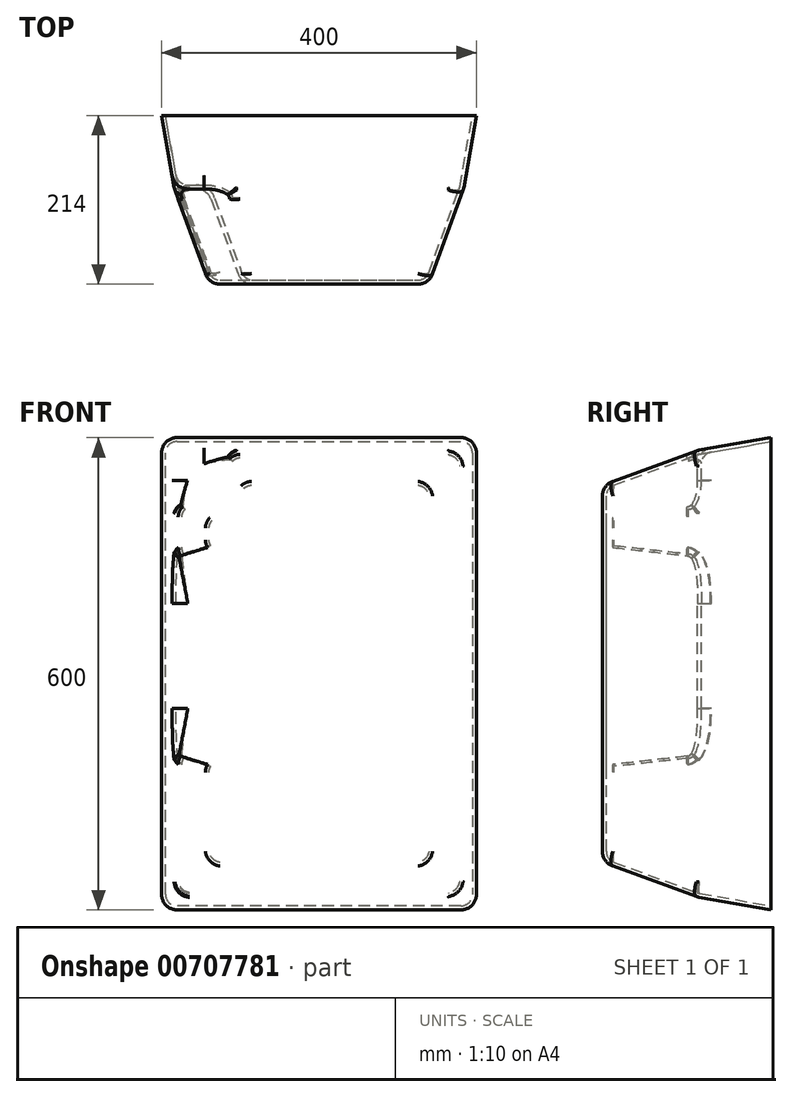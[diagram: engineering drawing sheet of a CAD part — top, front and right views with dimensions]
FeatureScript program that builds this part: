
annotation { "Feature Type Name" : "Feature", "Feature Type Description" : "" }
export const myFeature = defineFeature(function(context is Context, id is Id, definition is map)
    precondition{}
    {
        {
            var Q0;
            Q0=qCreatedBy(makeId("Front.planeOp"),FACE);
            var sketch = newSketch(context, id + "F0", { "sketchPlane" : qUnion([Q0])});
            skCircle(sketch, "E0", {"center": v(0, 0) * mm, "radius": 100 * mm});
            skLineSegment(sketch, "E1.bottom", {"start": v(-200, 300) * mm, "end": v(200, 300) * mm});
            skLineSegment(sketch, "E1.top", {"start": v(-200, -300) * mm, "end": v(200, -300) * mm});
            skLineSegment(sketch, "E1.left", {"start": v(-200, 300) * mm, "end": v(-200, -300) * mm});
            skLineSegment(sketch, "E1.right", {"start": v(200, 300) * mm, "end": v(200, -300) * mm});
            skSolve(sketch);
        }
        {
            var Q0;
            Q0=makeQuery(id+"F0.imprint","IMPRINT",FACE,{"disambiguationData":[TD([[makeQuery(id+"F0.imprint","IMPRINT",EDGE,{"derivedFrom":sQuery(id+"F0.wireOp",EDGE,"E0")}),-1.0]])]});
            var Q1;
            Q1=makeQuery(id+"F0.imprint","IMPRINT",FACE,{"disambiguationData":[TD([[makeQuery(id+"F0.imprint","IMPRINT",EDGE,{"derivedFrom":sQuery(id+"F0.wireOp",EDGE,"E0")}),1.0]])]});
            extrude(context, id + "F1", {"entities" : qUnion([Q0, Q1]), "depth" : 93 * mm, "offsetDistance" : 25 * mm, "hasDraft" : true, "draftAngle" : 10 * degree, "draftPullDirection" : true});
        }
        {
            var Q0;
            Q0=makeQuery(id+"F1.opExtrude","CAP_FACE",FACE,{"disambiguationData":[OSD([sQuery(id+"F0.wireOp",EDGE,"E1.bottom"),sQuery(id+"F0.wireOp",EDGE,"E1.top"),sQuery(id+"F0.wireOp",EDGE,"E1.left"),sQuery(id+"F0.wireOp",EDGE,"E1.right")])],"isStart":false});
            var sketch = newSketch(context, id + "F2", { "sketchPlane" : qUnion([Q0])});
            skLineSegment(sketch, "E2", {"start": v(-209.11, 182.83) * mm, "end": v(-67.8, 326.25) * mm});
            skLineSegment(sketch, "E3", {"start": v(99.21, 69.27) * mm, "end": v(99.21, -109.47) * mm});
            skLineSegment(sketch, "E4", {"start": v(-122.2, -49.55) * mm, "end": v(19.1, 93.87) * mm});
            skCircle(sketch, "E5", {"center": v(-72.45, -175.48) * mm, "radius": 40.45 * mm});
            skCircle(sketch, "E6", {"center": v(-367.03, 22.56) * mm, "radius": 67.26 * mm});
            skCircle(sketch, "E7", {"center": v(-367.03, 22.56) * mm, "radius": 225 * mm});
            skSolve(sketch);
        }
        {
            var Q0;
            Q0=makeQuery(id+"F2.imprint","IMPRINT",FACE,{"disambiguationData":[TD([[makeQuery(id+"F2.imprint","IMPRINT",EDGE,{"derivedFrom":sQuery(id+"F2.wireOp",EDGE,"E5")}),-1.0]])]});
            var Q1;
            Q1=makeQuery(id+"F2.imprint","IMPRINT",FACE,{"disambiguationData":[TD([[makeQuery(id+"F2.imprint","IMPRINT",EDGE,{"derivedFrom":sQuery(id+"F2.wireOp",EDGE,"E5")}),1.0]])]});
            extrude(context, id + "F3", {"entities" : qUnion([Q0, Q1]), "operationType" : NewBodyOperationType.ADD, "depth" : 121 * mm, "offsetDistance" : 25 * mm, "hasDraft" : true, "draftAngle" : 20 * degree, "draftPullDirection" : true});
        }
        {
            var Q0;
            Q0=makeQuery(id+"F3.opExtrude","CAP_FACE",FACE,{"disambiguationData":[OSD([sQuery(id+"F0.wireOp",EDGE,"E1.bottom"),sQuery(id+"F0.wireOp",EDGE,"E1.top"),sQuery(id+"F0.wireOp",EDGE,"E1.left"),sQuery(id+"F0.wireOp",EDGE,"E1.right"),sQuery(id+"F2.wireOp",EDGE,"E2"),sQuery(id+"F2.wireOp",EDGE,"E7")])],"isStart":false});
            var Q1;
            Q1=makeQuery(id+"F1.opExtrude","SWEPT_EDGE",EDGE,{"disambiguationData":[OSD([sQuery(id+"F0.wireOp",EDGE,"E1.top"),sQuery(id+"F0.wireOp",EDGE,"E1.right")])]});
            var Q2;
            {var subQ0=sQuery(id+"F0.wireOp",EDGE,"E1.left");var subQ1=makeQuery(id+"F1.opExtrude","CAP_EDGE",EDGE,{"disambiguationData":[OSD([subQ0])],"isStart":false});Q2=makeQuery(id+"F3.opExtrude","SWEPT_FACE",FACE,{"disambiguationData":[OSD([subQ0]),TDD([makeQuery(id+"F2.imprint","IMPRINT",EDGE,{"disambiguationData":[TD([[makeQuery(id+"F2.imprint","INTERSECT",VERTEX,{"derivedFrom":[makeQuery(id+"F1.opExtrude","CAP_EDGE",EDGE,{"disambiguationData":[OSD([sQuery(id+"F0.wireOp",EDGE,"E1.top")])],"isStart":false}),subQ1]}),1.0]])],"derivedFrom":subQ1})])]});}
            var Q3;
            Q3=makeQuery(id+"F3.opExtrude","SWEPT_EDGE",EDGE,{"disambiguationData":[OSD([sQuery(id+"F0.wireOp",EDGE,"E1.top"),sQuery(id+"F0.wireOp",EDGE,"E1.right")])]});
            var Q4;
            Q4=makeQuery(id+"F3.opExtrude","SWEPT_FACE",FACE,{"disambiguationData":[OSD([sQuery(id+"F0.wireOp",EDGE,"E1.right")])]});
            var Q5;
            Q5=makeQuery(id+"F3.opExtrude","SWEPT_FACE",FACE,{"disambiguationData":[OSD([sQuery(id+"F0.wireOp",EDGE,"E1.top")])]});
            var Q6;
            Q6=makeQuery(id+"F3.opExtrude","SWEPT_EDGE",EDGE,{"disambiguationData":[OSD([sQuery(id+"F0.wireOp",EDGE,"E1.bottom"),sQuery(id+"F0.wireOp",EDGE,"E1.right")])]});
            var Q7;
            Q7=makeQuery(id+"F3.opExtrude","CAP_EDGE",EDGE,{"disambiguationData":[OSD([sQuery(id+"F2.wireOp",EDGE,"E7")])],"isStart":true});
            var Q8;
            Q8=makeQuery(id+"F3.opExtrude","SWEPT_FACE",FACE,{"disambiguationData":[OSD([sQuery(id+"F0.wireOp",EDGE,"E1.bottom")])]});
            var Q9;
            {var subQ0=sQuery(id+"F0.wireOp",EDGE,"E1.right");Q9=makeQuery(id+"F3.boolean.opBoolean","MERGE",EDGE,{"derivedFrom":[makeQuery(id+"F1.opExtrude","CAP_EDGE",EDGE,{"disambiguationData":[OSD([subQ0])],"isStart":false}),makeQuery(id+"F3.opExtrude","CAP_EDGE",EDGE,{"disambiguationData":[OSD([subQ0])],"isStart":true})]});}
            var Q10;
            {var subQ0=sQuery(id+"F0.wireOp",EDGE,"E1.left");var subQ1=sQuery(id+"F2.wireOp",EDGE,"E7");var subQ3=sQuery(id+"F0.wireOp",EDGE,"E1.top");Q10=makeQuery(id+"F3.boolean.opBoolean","SPLIT",FACE,{"disambiguationData":[TD([makeQuery(id+"F3.opExtrude","SWEPT_FACE",FACE,{"disambiguationData":[OSD([subQ1])]})])],"derivedFrom":makeQuery(id+"F1.opExtrude","CAP_FACE",FACE,{"disambiguationData":[OSD([sQuery(id+"F0.wireOp",EDGE,"E1.bottom"),subQ3,subQ0,sQuery(id+"F0.wireOp",EDGE,"E1.right")])],"isStart":false})});}
            var Q11;
            Q11=makeQuery(id+"F3.opExtrude","SWEPT_EDGE",EDGE,{"disambiguationData":[OSD([sQuery(id+"F0.wireOp",EDGE,"E1.bottom"),sQuery(id+"F2.wireOp",EDGE,"E2")])]});
            var Q12;
            Q12=makeQuery(id+"F1.opExtrude","SWEPT_EDGE",EDGE,{"disambiguationData":[OSD([sQuery(id+"F0.wireOp",EDGE,"E1.bottom"),sQuery(id+"F0.wireOp",EDGE,"E1.right")])]});
            var Q13;
            Q13=makeQuery(id+"F1.opExtrude","SWEPT_EDGE",EDGE,{"disambiguationData":[OSD([sQuery(id+"F0.wireOp",EDGE,"E1.bottom"),sQuery(id+"F0.wireOp",EDGE,"E1.left")])]});
            var Q14;
            {var subQ0=sQuery(id+"F2.wireOp",EDGE,"E7");var subQ1=sQuery(id+"F0.wireOp",EDGE,"E1.left");Q14=makeQuery(id+"F3.opExtrude","SWEPT_EDGE",EDGE,{"disambiguationData":[OSD([subQ1,subQ0]),TDD([makeQuery(id+"F2.imprint","INTERSECT",VERTEX,{"disambiguationData":[OD(0.0)],"derivedFrom":[makeQuery(id+"F1.opExtrude","CAP_EDGE",EDGE,{"disambiguationData":[OSD([subQ1])],"isStart":false}),subQ0]})])]});}
            var Q15;
            Q15=makeQuery(id+"F3.opExtrude","SWEPT_FACE",FACE,{"disambiguationData":[OSD([sQuery(id+"F2.wireOp",EDGE,"E7")])]});
            var Q16;
            {var subQ0=sQuery(id+"F0.wireOp",EDGE,"E1.left");var subQ1=makeQuery(id+"F1.opExtrude","CAP_EDGE",EDGE,{"disambiguationData":[OSD([subQ0])],"isStart":false});Q16=makeQuery(id+"F3.boolean.opBoolean","MERGE",EDGE,{"derivedFrom":[subQ1,makeQuery(id+"F3.opExtrude","CAP_EDGE",EDGE,{"disambiguationData":[OSD([subQ0]),TDD([makeQuery(id+"F2.imprint","IMPRINT",EDGE,{"disambiguationData":[TD([[makeQuery(id+"F2.imprint","INTERSECT",VERTEX,{"derivedFrom":[makeQuery(id+"F1.opExtrude","CAP_EDGE",EDGE,{"disambiguationData":[OSD([sQuery(id+"F0.wireOp",EDGE,"E1.top")])],"isStart":false}),subQ1]}),1.0]])],"derivedFrom":subQ1})])],"isStart":true})]});}
            var Q17;
            {var subQ0=sQuery(id+"F0.wireOp",EDGE,"E1.left");var subQ1=makeQuery(id+"F1.opExtrude","CAP_EDGE",EDGE,{"disambiguationData":[OSD([subQ0])],"isStart":false});Q17=makeQuery(id+"F3.opExtrude","SWEPT_FACE",FACE,{"disambiguationData":[OSD([subQ0]),TDD([makeQuery(id+"F2.imprint","IMPRINT",EDGE,{"disambiguationData":[TD([[makeQuery(id+"F2.imprint","INTERSECT",VERTEX,{"derivedFrom":[subQ1,sQuery(id+"F2.wireOp",EDGE,"E2")]}),-1.0]])],"derivedFrom":subQ1})])]});}
            var Q18;
            Q18=makeQuery(id+"F3.opExtrude","SWEPT_EDGE",EDGE,{"disambiguationData":[OSD([sQuery(id+"F0.wireOp",EDGE,"E1.left"),sQuery(id+"F2.wireOp",EDGE,"E2")])]});
            var Q19;
            Q19=makeQuery(id+"F3.opExtrude","SWEPT_FACE",FACE,{"disambiguationData":[OSD([sQuery(id+"F2.wireOp",EDGE,"E2")])]});
            var Q20;
            {var subQ0=sQuery(id+"F2.wireOp",EDGE,"E7");var subQ1=sQuery(id+"F0.wireOp",EDGE,"E1.left");Q20=makeQuery(id+"F3.opExtrude","SWEPT_EDGE",EDGE,{"disambiguationData":[OSD([subQ1,subQ0]),TDD([makeQuery(id+"F2.imprint","INTERSECT",VERTEX,{"disambiguationData":[OD(1.0)],"derivedFrom":[makeQuery(id+"F1.opExtrude","CAP_EDGE",EDGE,{"disambiguationData":[OSD([subQ1])],"isStart":false}),subQ0]})])]});}
            var Q21;
            {var subQ0=sQuery(id+"F0.wireOp",EDGE,"E1.left");var subQ1=makeQuery(id+"F1.opExtrude","CAP_EDGE",EDGE,{"disambiguationData":[OSD([subQ0])],"isStart":false});Q21=makeQuery(id+"F3.boolean.opBoolean","MERGE",EDGE,{"derivedFrom":[subQ1,makeQuery(id+"F3.opExtrude","CAP_EDGE",EDGE,{"disambiguationData":[OSD([subQ0]),TDD([makeQuery(id+"F2.imprint","IMPRINT",EDGE,{"disambiguationData":[TD([[makeQuery(id+"F2.imprint","INTERSECT",VERTEX,{"derivedFrom":[subQ1,sQuery(id+"F2.wireOp",EDGE,"E2")]}),-1.0]])],"derivedFrom":subQ1})])],"isStart":true})]});}
            var Q22;
            {var subQ0=sQuery(id+"F0.wireOp",EDGE,"E1.left");var subQ1=makeQuery(id+"F1.opExtrude","CAP_EDGE",EDGE,{"disambiguationData":[OSD([subQ0])],"isStart":false});var subQ3=sQuery(id+"F2.wireOp",EDGE,"E7");Q22=makeQuery(id+"F3.boolean.opBoolean","SPLIT",EDGE,{"disambiguationData":[TD([makeQuery(id+"F3.opExtrude","SWEPT_FACE",FACE,{"disambiguationData":[OSD([subQ3])]})])],"derivedFrom":subQ1});}
            var Q23;
            {var subQ0=sQuery(id+"F0.wireOp",EDGE,"E1.bottom");var subQ2=sQuery(id+"F0.wireOp",EDGE,"E1.left");Q23=makeQuery(id+"F3.boolean.opBoolean","SPLIT",FACE,{"disambiguationData":[TD([makeQuery(id+"F1.opExtrude","SWEPT_FACE",FACE,{"disambiguationData":[OSD([subQ0])]})])],"derivedFrom":makeQuery(id+"F1.opExtrude","CAP_FACE",FACE,{"disambiguationData":[OSD([subQ0,sQuery(id+"F0.wireOp",EDGE,"E1.top"),subQ2,sQuery(id+"F0.wireOp",EDGE,"E1.right")])],"isStart":false})});}
            var Q24;
            {var subQ0=sQuery(id+"F0.wireOp",EDGE,"E1.bottom");Q24=makeQuery(id+"F3.boolean.opBoolean","MERGE",EDGE,{"derivedFrom":[makeQuery(id+"F1.opExtrude","CAP_EDGE",EDGE,{"disambiguationData":[OSD([subQ0])],"isStart":false}),makeQuery(id+"F3.opExtrude","CAP_EDGE",EDGE,{"disambiguationData":[OSD([subQ0])],"isStart":true})]});}
            var Q25;
            Q25=makeQuery(id+"F3.boolean.opBoolean","SPLIT",EDGE,{"derivedFrom":makeQuery(id+"F1.opExtrude","CAP_EDGE",EDGE,{"disambiguationData":[OSD([sQuery(id+"F0.wireOp",EDGE,"E1.bottom")])],"isStart":false})});
            var Q26;
            Q26=makeQuery(id+"F3.opExtrude","CAP_EDGE",EDGE,{"disambiguationData":[OSD([sQuery(id+"F2.wireOp",EDGE,"E2")])],"isStart":true});
            var Q27;
            {var subQ1=sQuery(id+"F0.wireOp",EDGE,"E1.left");var subQ2=sQuery(id+"F0.wireOp",EDGE,"E1.bottom");var subQ3=makeQuery(id+"F1.opExtrude","CAP_EDGE",EDGE,{"disambiguationData":[OSD([subQ1])],"isStart":false});Q27=makeQuery(id+"F3.boolean.opBoolean","SPLIT",EDGE,{"disambiguationData":[TD([makeQuery(id+"F1.opExtrude","SWEPT_FACE",FACE,{"disambiguationData":[OSD([subQ2])]})])],"derivedFrom":subQ3});}
            var Q28;
            Q28=makeQuery(id+"F3.opExtrude","SWEPT_EDGE",EDGE,{"disambiguationData":[OSD([sQuery(id+"F0.wireOp",EDGE,"E1.top"),sQuery(id+"F0.wireOp",EDGE,"E1.left")])]});
            var Q29;
            Q29=makeQuery(id+"F1.opExtrude","SWEPT_EDGE",EDGE,{"disambiguationData":[OSD([sQuery(id+"F0.wireOp",EDGE,"E1.top"),sQuery(id+"F0.wireOp",EDGE,"E1.left")])]});
            var Q30;
            {var subQ0=sQuery(id+"F0.wireOp",EDGE,"E1.top");Q30=makeQuery(id+"F3.boolean.opBoolean","MERGE",EDGE,{"derivedFrom":[makeQuery(id+"F1.opExtrude","CAP_EDGE",EDGE,{"disambiguationData":[OSD([subQ0])],"isStart":false}),makeQuery(id+"F3.opExtrude","CAP_EDGE",EDGE,{"disambiguationData":[OSD([subQ0])],"isStart":true})]});}
            fillet(context, id + "F4", {"entities" : qUnion([Q0, Q1, Q2, Q3, Q4, Q5, Q6, Q7, Q8, Q9, Q10, Q11, Q12, Q13, Q14, Q15, Q16, Q17, Q18, Q19, Q20, Q21, Q22, Q23, Q24, Q25, Q26, Q27, Q28, Q29, Q30]), "radius" : 20 * mm, "tangentPropagation" : true, "allowEdgeOverflow" : false});
        }
        {
            var Q0;
            Q0=makeQuery(id+"F1.opExtrude","CAP_FACE",FACE,{"disambiguationData":[OSD([sQuery(id+"F0.wireOp",EDGE,"E1.bottom"),sQuery(id+"F0.wireOp",EDGE,"E1.top"),sQuery(id+"F0.wireOp",EDGE,"E1.left"),sQuery(id+"F0.wireOp",EDGE,"E1.right")])],"isStart":true});
            shell(context, id + "F5", {"entities" : qUnion([Q0]), "thickness" : 5 * mm});
        }
    });
